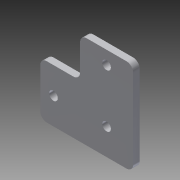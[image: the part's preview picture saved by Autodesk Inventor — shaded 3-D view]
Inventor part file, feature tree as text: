
AUTODESK INVENTOR PART (.ipt)
format: ipt  version: 2014 (Build 180170000, 170)  size: 97,792 bytes
history: native  units: in
note: dims shown in document units (in); Inventor stores cm internally (conversion verified against a paired STEP export)
features: extrude x1, fillet x1, sketch x1
ambient origin geometry x8: Origin, YZ Plane, XZ Plane, XY Plane, X Axis, Y Axis, Z Axis, Center Point
bodies: Solid1 (feature_tree)
feature tree (3):
  extrude  "Extrusion1"  Depth=1.0in
  fillet  "Fillet1"  Radius=0.163in
  sketch  "Sketch1"  dims[d0=1.75in d1=1.0in d2=0.163in d3=0.5in d4=0.25in d5=0.7874in d7=1.0in d8=0.3937in d10=1.0in d12=0.7874in d14=1.0in d15=0.3937in d17=1.0in d19=0.125in d20=0.0in d21=0.125in]
